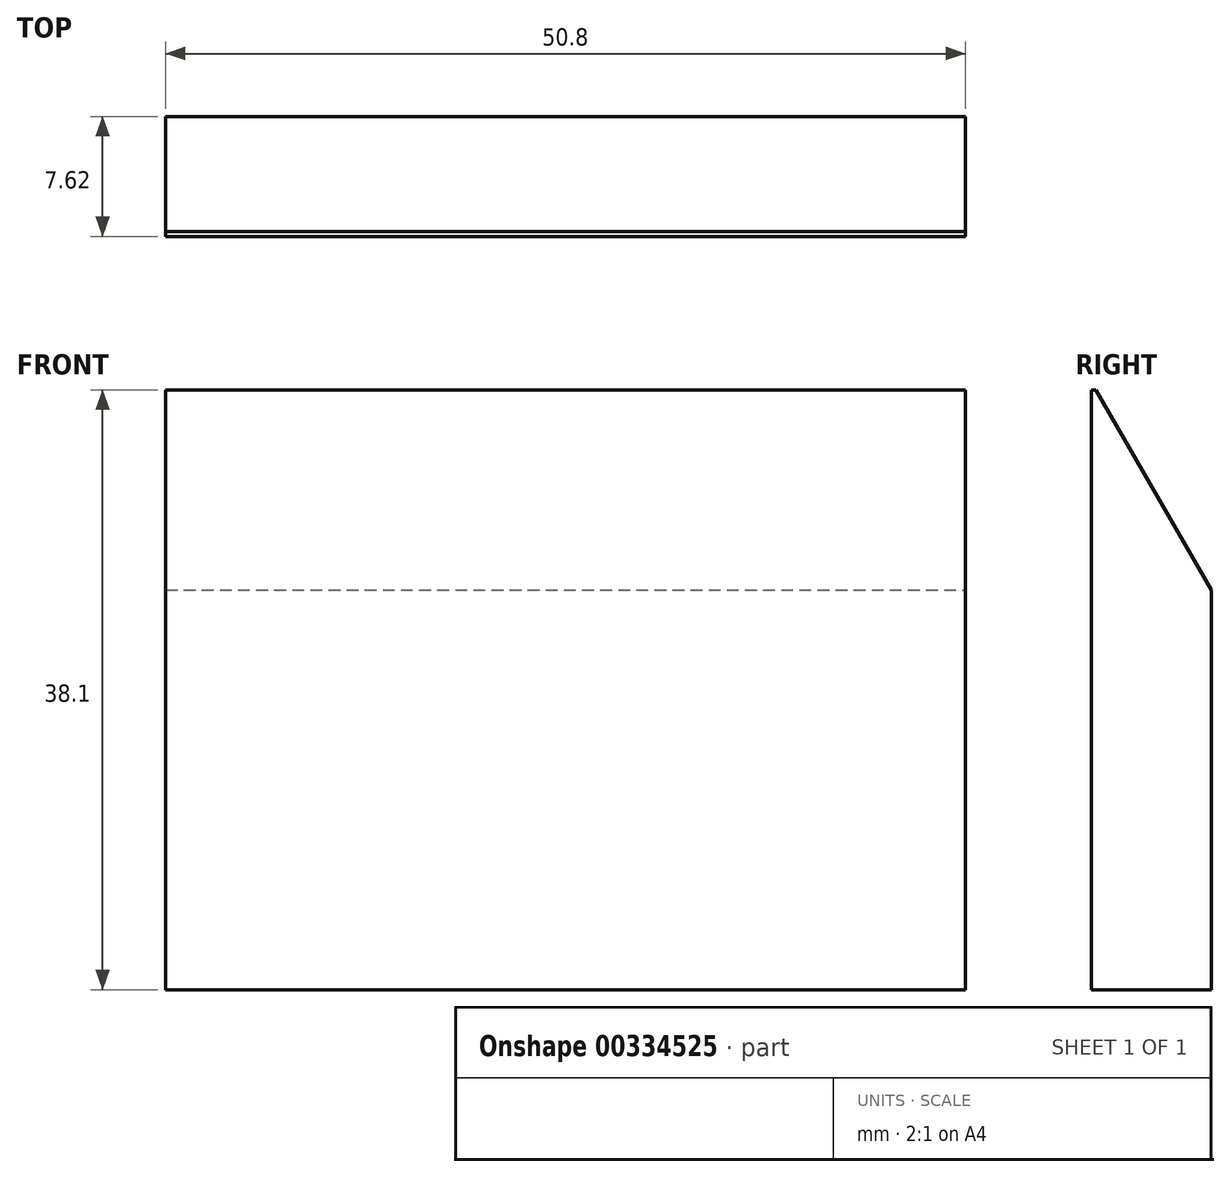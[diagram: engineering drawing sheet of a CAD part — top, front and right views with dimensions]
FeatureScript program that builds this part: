
annotation { "Feature Type Name" : "Feature", "Feature Type Description" : "" }
export const myFeature = defineFeature(function(context is Context, id is Id, definition is map)
    precondition{}
    {
        {
            var Q0;
            Q0=qCreatedBy(makeId("Front.planeOp"),FACE);
            var sketch = newSketch(context, id + "F0", { "sketchPlane" : qUnion([Q0])});
            skLineSegment(sketch, "E0.bottom", {"start": v(-50.8, 55.44) * mm, "end": v(0, 55.44) * mm});
            skLineSegment(sketch, "E0.top", {"start": v(-50.8, 17.34) * mm, "end": v(0, 17.34) * mm});
            skLineSegment(sketch, "E0.left", {"start": v(-50.8, 55.44) * mm, "end": v(-50.8, 17.34) * mm});
            skLineSegment(sketch, "E0.right", {"start": v(0, 55.44) * mm, "end": v(0, 17.34) * mm});
            skSolve(sketch);
        }
        {
            var Q0;
            Q0 = qSketchRegion(id + "F0", true);
            extrude(context, id + "F1", {"entities" : qUnion([Q0]), "depth" : 7.62 * mm});
        }
        {
            var Q0;
            Q0=makeQuery(id+"F1.opExtrude","CAP_EDGE",EDGE,{"disambiguationData":[OSD([sQuery(id+"F0.wireOp",EDGE,"E0.bottom")])],"isStart":true});
            chamfer(context, id + "F2", {"entities" : qUnion([Q0]), "chamferType" : ChamferType.OFFSET_ANGLE, "width" : 12.7 * mm, "oppositeDirection" : false, "angle" : 30 * degree, "tangentPropagation" : true});
        }
    });
